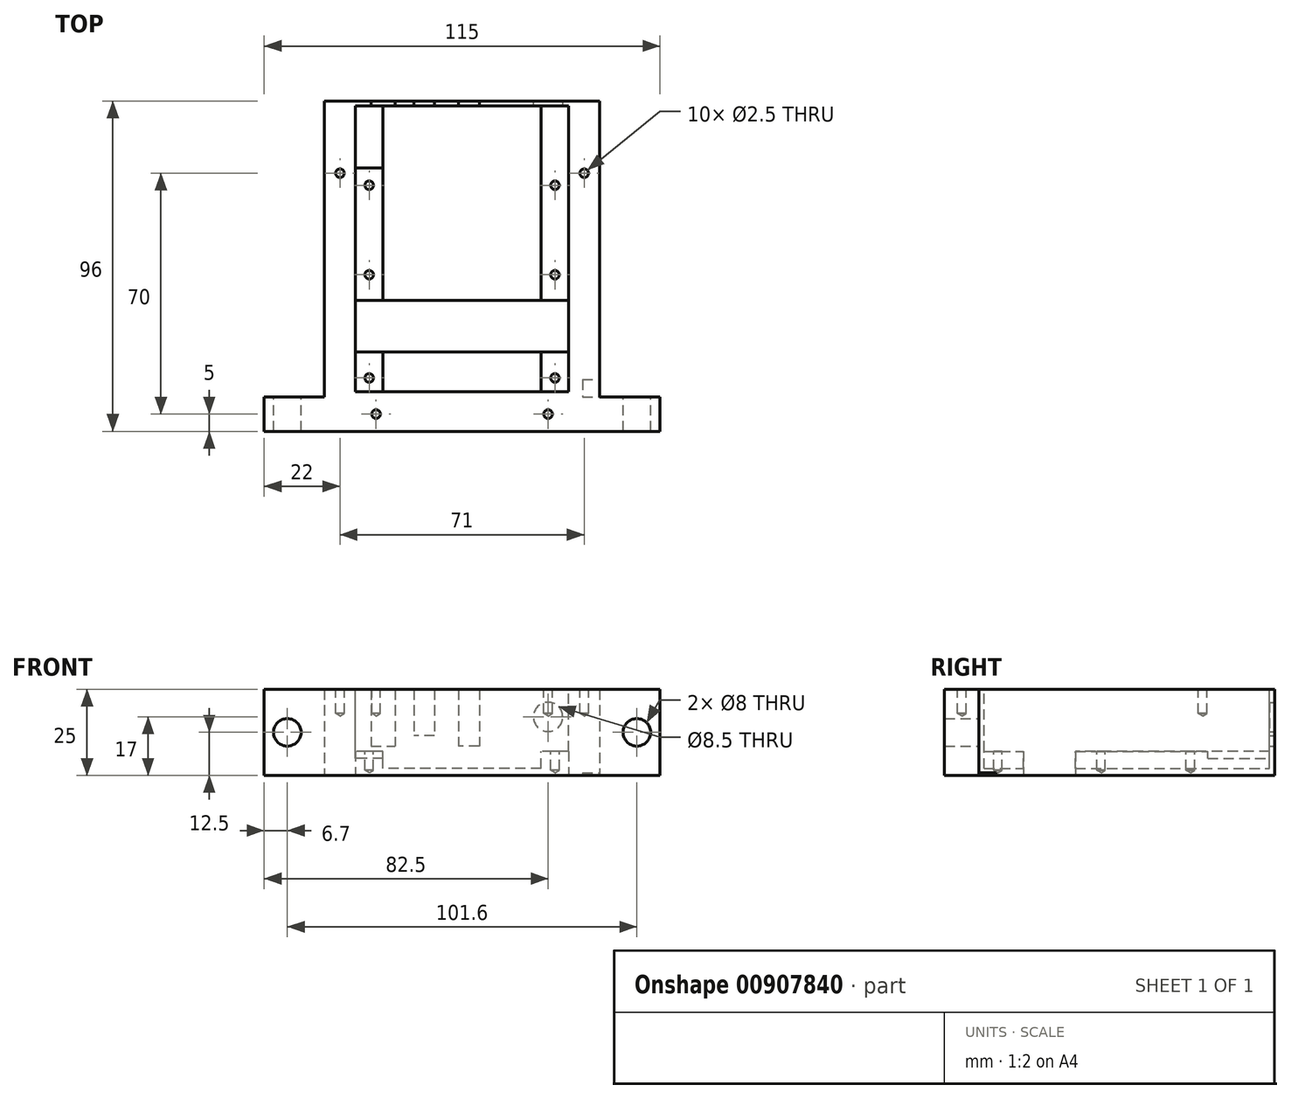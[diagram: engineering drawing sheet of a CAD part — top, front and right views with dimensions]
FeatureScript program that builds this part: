
annotation { "Feature Type Name" : "Feature", "Feature Type Description" : "" }
export const myFeature = defineFeature(function(context is Context, id is Id, definition is map)
    precondition{}
    {
        {
            var Q0;
            Q0=qCreatedBy(makeId("Top.planeOp"),FACE);
            var sketch = newSketch(context, id + "F0", { "sketchPlane" : qUnion([Q0])});
            skLineSegment(sketch, "E0.bottom", {"start": v(-40, 48) * mm, "end": v(40, 48) * mm});
            skLineSegment(sketch, "E0.left", {"start": v(-40, 48) * mm, "end": v(-40, -38) * mm});
            skLineSegment(sketch, "E0.right", {"start": v(40, 48) * mm, "end": v(40, -38) * mm});
            skLineSegment(sketch, "E1.bottom", {"start": v(-57.5, -38) * mm, "end": v(-40, -38) * mm});
            skLineSegment(sketch, "E1.top", {"start": v(-57.5, -48) * mm, "end": v(57.5, -48) * mm});
            skLineSegment(sketch, "E1.left", {"start": v(-57.5, -38) * mm, "end": v(-57.5, -48) * mm});
            skLineSegment(sketch, "E1.right", {"start": v(57.5, -38) * mm, "end": v(57.5, -48) * mm});
            skLineSegment(sketch, "E2", {"start": v(0, 66.03) * mm, "end": v(0, -67.52) * mm, "construction": true});
            skLineSegment(sketch, "E3.trimOffspring", {"start": v(40, -38) * mm, "end": v(57.5, -38) * mm});
            skLineSegment(sketch, "E4", {"start": v(-41.52, 0) * mm, "end": v(40.59, 0) * mm, "construction": true});
            skSolve(sketch);
        }
        {
            var Q0;
            Q0 = qSketchRegion(id + "F0", true);
            extrude(context, id + "F1", {"entities" : qUnion([Q0]), "depth" : 25 * mm, "offsetDistance" : 25 * mm});
        }
        {
            var Q0;
            Q0=makeQuery(id+"F1.opExtrude","CAP_FACE",FACE,{"disambiguationData":[OSD([sQuery(id+"F0.wireOp",EDGE,"E0.bottom"),sQuery(id+"F0.wireOp",EDGE,"E0.left"),sQuery(id+"F0.wireOp",EDGE,"E0.right"),sQuery(id+"F0.wireOp",EDGE,"E1.bottom"),sQuery(id+"F0.wireOp",EDGE,"E1.top"),sQuery(id+"F0.wireOp",EDGE,"E1.left"),sQuery(id+"F0.wireOp",EDGE,"E1.right"),sQuery(id+"F0.wireOp",EDGE,"E3.trimOffspring")])],"isStart":false});
            var sketch = newSketch(context, id + "F2", { "sketchPlane" : qUnion([Q0])});
            skLineSegment(sketch, "E5", {"start": v(0, 48) * mm, "end": v(0, -48) * mm, "construction": true});
            skLineSegment(sketch, "E6", {"start": v(-40, 5) * mm, "end": v(40, 5) * mm, "construction": true});
            skLineSegment(sketch, "E7.bottom", {"start": v(31, 46.5) * mm, "end": v(-31, 46.5) * mm});
            skLineSegment(sketch, "E7.top", {"start": v(31, -36.5) * mm, "end": v(-31, -36.5) * mm});
            skLineSegment(sketch, "E7.left", {"start": v(31, 46.5) * mm, "end": v(31, -36.5) * mm});
            skLineSegment(sketch, "E7.right", {"start": v(-31, 46.5) * mm, "end": v(-31, -36.5) * mm});
            skPoint(sketch, "E7.middle", {"position": v(0, 5) * mm});
            skSolve(sketch);
        }
        {
            var Q0;
            Q0=makeQuery(id+"F2.imprint","IMPRINT",FACE,{"disambiguationData":[TD([[makeQuery(id+"F2.imprint","IMPRINT",EDGE,{"derivedFrom":sQuery(id+"F2.wireOp",EDGE,"E7.bottom")}),1.0]])]});
            extrude(context, id + "F3", {"entities" : qUnion([Q0]), "operationType" : NewBodyOperationType.REMOVE, "oppositeDirection" : true, "depth" : 18 * mm, "offsetDistance" : 25 * mm});
        }
        {
            var Q0;
            Q0=makeQuery(id+"F3.boolean.opBoolean","COPY",FACE,{"derivedFrom":makeQuery(id+"F3.opExtrude","CAP_FACE",FACE,{"disambiguationData":[OSD([sQuery(id+"F2.wireOp",EDGE,"E7.bottom"),sQuery(id+"F2.wireOp",EDGE,"E7.top"),sQuery(id+"F2.wireOp",EDGE,"E7.left"),sQuery(id+"F2.wireOp",EDGE,"E7.right")])],"isStart":false})});
            var sketch = newSketch(context, id + "F4", { "sketchPlane" : qUnion([Q0])});
            skLineSegment(sketch, "E8", {"start": v(0, 46.5) * mm, "end": v(0, -36.5) * mm, "construction": true});
            skLineSegment(sketch, "E9.bottom", {"start": v(23, -36.5) * mm, "end": v(-23, -36.5) * mm});
            skLineSegment(sketch, "E9.top", {"start": v(23, 46.5) * mm, "end": v(-23, 46.5) * mm});
            skLineSegment(sketch, "E9.left", {"start": v(23, -36.5) * mm, "end": v(23, 46.5) * mm});
            skLineSegment(sketch, "E9.right", {"start": v(-23, -36.5) * mm, "end": v(-23, 46.5) * mm});
            skSolve(sketch);
        }
        {
            var Q0;
            Q0=makeQuery(id+"F4.imprint","IMPRINT",FACE,{"disambiguationData":[TD([[makeQuery(id+"F4.imprint","IMPRINT",EDGE,{"derivedFrom":sQuery(id+"F4.wireOp",EDGE,"E9.bottom")}),-1.0]])]});
            extrude(context, id + "F5", {"entities" : qUnion([Q0]), "operationType" : NewBodyOperationType.REMOVE, "oppositeDirection" : true, "depth" : 5 * mm, "offsetDistance" : 25 * mm});
        }
        {
            var Q0;
            Q0=makeQuery(id+"F3.boolean.opBoolean","COPY",FACE,{"derivedFrom":makeQuery(id+"F3.opExtrude","CAP_FACE",FACE,{"disambiguationData":[OSD([sQuery(id+"F2.wireOp",EDGE,"E7.bottom"),sQuery(id+"F2.wireOp",EDGE,"E7.top"),sQuery(id+"F2.wireOp",EDGE,"E7.left"),sQuery(id+"F2.wireOp",EDGE,"E7.right")])],"isStart":false})});
            var sketch = newSketch(context, id + "F6", { "sketchPlane" : qUnion([Q0])});
            skLineSegment(sketch, "E10", {"start": v(-27, -36.5) * mm, "end": v(-27, 28.23) * mm, "construction": true});
            skLineSegment(sketch, "E11", {"start": v(27, -36.5) * mm, "end": v(27, 26.7) * mm, "construction": true});
            skLineSegment(sketch, "E12", {"start": v(0, 28) * mm, "end": v(0, -50.3) * mm, "construction": true});
            skLineSegment(sketch, "E13", {"start": v(-29.07, 23.5) * mm, "end": v(28.49, 23.5) * mm, "construction": true});
            skLineSegment(sketch, "E14.0", {"start": v(-29.07, -2.5) * mm, "end": v(28.49, -2.5) * mm});
            skLineSegment(sketch, "E15.0", {"start": v(-29.07, -32.5) * mm, "end": v(28.49, -32.5) * mm});
            skPoint(sketch, "E16", {"position": v(-27, -32.5) * mm});
            skPoint(sketch, "E17", {"position": v(-27, 23.5) * mm});
            skPoint(sketch, "E18", {"position": v(27, 23.5) * mm});
            skPoint(sketch, "E19", {"position": v(27, -2.5) * mm});
            skPoint(sketch, "E20", {"position": v(27, -32.5) * mm});
            skPoint(sketch, "E21", {"position": v(-27, -2.5) * mm});
            skSolve(sketch);
        }
        {
            var Q0;
            Q0=sQuery(id+"F6.wireOp",VERTEX,"E16");
            var Q1;
            Q1=sQuery(id+"F6.wireOp",VERTEX,"E21");
            var Q2;
            Q2=sQuery(id+"F6.wireOp",VERTEX,"E17");
            var Q3;
            Q3=sQuery(id+"F6.wireOp",VERTEX,"E20");
            var Q4;
            Q4=sQuery(id+"F6.wireOp",VERTEX,"E19");
            var Q5;
            Q5=sQuery(id+"F6.wireOp",VERTEX,"E18");
            var Q6;
            Q6=makeQuery(id+"F1.opExtrude","SWEPT_BODY",BODY,{"disambiguationData":[OSD([sQuery(id+"F0.wireOp",EDGE,"E0.bottom"),sQuery(id+"F0.wireOp",EDGE,"E0.left"),sQuery(id+"F0.wireOp",EDGE,"E0.right"),sQuery(id+"F0.wireOp",EDGE,"E1.bottom"),sQuery(id+"F0.wireOp",EDGE,"E1.top"),sQuery(id+"F0.wireOp",EDGE,"E1.left"),sQuery(id+"F0.wireOp",EDGE,"E1.right"),sQuery(id+"F0.wireOp",EDGE,"E3.trimOffspring")])]});
            hole(context, id + "F7", {"style" : HoleStyle.SIMPLE, "endStyle" : HoleEndStyle.BLIND, "holeDiameter" : 2.5 * mm, "majorDiameter" : 5 * mm, "holeDepth" : 5.5 * mm, "isTappedThrough" : true, "tappedDepth" : 12 * mm, "tapClearance" : 3, "startFromSketch" : true, "locations" : qUnion([Q0, Q1, Q2, Q3, Q4, Q5]), "scope" : qUnion([Q6])});
        }
        {
            var Q0;
            Q0=makeQuery(id+"F1.opExtrude","CAP_FACE",FACE,{"disambiguationData":[OSD([sQuery(id+"F0.wireOp",EDGE,"E0.bottom"),sQuery(id+"F0.wireOp",EDGE,"E0.left"),sQuery(id+"F0.wireOp",EDGE,"E0.right"),sQuery(id+"F0.wireOp",EDGE,"E1.bottom"),sQuery(id+"F0.wireOp",EDGE,"E1.top"),sQuery(id+"F0.wireOp",EDGE,"E1.left"),sQuery(id+"F0.wireOp",EDGE,"E1.right"),sQuery(id+"F0.wireOp",EDGE,"E3.trimOffspring")])],"isStart":true});
            var sketch = newSketch(context, id + "F8", { "sketchPlane" : qUnion([Q0])});
            skLineSegment(sketch, "E22.bottom", {"start": v(-31, 25) * mm, "end": v(31, 25) * mm});
            skLineSegment(sketch, "E22.top", {"start": v(-31, 10) * mm, "end": v(31, 10) * mm});
            skLineSegment(sketch, "E22.left", {"start": v(-31, 25) * mm, "end": v(-31, 10) * mm});
            skLineSegment(sketch, "E22.right", {"start": v(31, 25) * mm, "end": v(31, 10) * mm});
            skPoint(sketch, "E23.endSnap0", {"position": v(0, 10) * mm});
            skLineSegment(sketch, "E24", {"start": v(0, 48) * mm, "end": v(0, 0) * mm, "construction": true});
            skSolve(sketch);
        }
        {
            var Q0;
            Q0=makeQuery(id+"F8.imprint","IMPRINT",FACE,{"disambiguationData":[TD([[makeQuery(id+"F8.imprint","IMPRINT",EDGE,{"derivedFrom":sQuery(id+"F8.wireOp",EDGE,"E22.bottom")}),-1.0]])]});
            extrude(context, id + "F9", {"entities" : qUnion([Q0]), "operationType" : NewBodyOperationType.REMOVE, "endBound" : BoundingType.THROUGH_ALL, "oppositeDirection" : true, "depth" : 25 * mm, "offsetDistance" : 25 * mm});
        }
        {
            var Q0;
            Q0=makeQuery(id+"F1.opExtrude","SWEPT_FACE",FACE,{"disambiguationData":[OSD([sQuery(id+"F0.wireOp",EDGE,"E3.trimOffspring")])]});
            var sketch = newSketch(context, id + "F10", { "sketchPlane" : qUnion([Q0])});
            skLineSegment(sketch, "E25", {"start": v(-51.24, 12.5) * mm, "end": v(51.38, 12.5) * mm, "construction": true});
            skLineSegment(sketch, "E26", {"start": v(50.8, 1.14) * mm, "end": v(50.8, 21.87) * mm, "construction": true});
            skLineSegment(sketch, "E27", {"start": v(-50.8, 2.75) * mm, "end": v(-50.8, 19.82) * mm, "construction": true});
            skLineSegment(sketch, "E28", {"start": v(0, 27.92) * mm, "end": v(0, 18.42) * mm, "construction": true});
            skPoint(sketch, "E29", {"position": v(50.8, 12.5) * mm});
            skPoint(sketch, "E30", {"position": v(-50.8, 12.5) * mm});
            skSolve(sketch);
        }
        {
            var Q0;
            Q0=sQuery(id+"F10.wireOp",VERTEX,"E29");
            var Q1;
            Q1=sQuery(id+"F10.wireOp",VERTEX,"E30");
            var Q2;
            Q2=makeQuery(id+"F1.opExtrude","SWEPT_BODY",BODY,{"disambiguationData":[OSD([sQuery(id+"F0.wireOp",EDGE,"E0.bottom"),sQuery(id+"F0.wireOp",EDGE,"E0.left"),sQuery(id+"F0.wireOp",EDGE,"E0.right"),sQuery(id+"F0.wireOp",EDGE,"E1.bottom"),sQuery(id+"F0.wireOp",EDGE,"E1.top"),sQuery(id+"F0.wireOp",EDGE,"E1.left"),sQuery(id+"F0.wireOp",EDGE,"E1.right"),sQuery(id+"F0.wireOp",EDGE,"E3.trimOffspring")])]});
            hole(context, id + "F11", {"style" : HoleStyle.SIMPLE, "endStyle" : HoleEndStyle.THROUGH, "holeDiameter" : 8 * mm, "majorDiameter" : 5 * mm, "isTappedThrough" : true, "tappedDepth" : 12 * mm, "tapClearance" : 3, "startFromSketch" : true, "locations" : qUnion([Q0, Q1]), "scope" : qUnion([Q2])});
        }
        {
            var Q0;
            Q0=makeQuery(id+"F1.opExtrude","SWEPT_FACE",FACE,{"disambiguationData":[OSD([sQuery(id+"F0.wireOp",EDGE,"E0.bottom")])]});
            var sketch = newSketch(context, id + "F12", { "sketchPlane" : qUnion([Q0])});
            skLineSegment(sketch, "E31.bottom", {"start": v(26.5, 25) * mm, "end": v(19.5, 25) * mm});
            skLineSegment(sketch, "E31.top", {"start": v(26.5, 8.5) * mm, "end": v(19.5, 8.5) * mm});
            skLineSegment(sketch, "E31.left", {"start": v(26.5, 25) * mm, "end": v(26.5, 8.5) * mm});
            skLineSegment(sketch, "E31.right", {"start": v(19.5, 25) * mm, "end": v(19.5, 8.5) * mm});
            skLineSegment(sketch, "E32.bottom", {"start": v(8, 25) * mm, "end": v(14, 25) * mm});
            skLineSegment(sketch, "E32.left", {"start": v(8, 25) * mm, "end": v(8, 11.5) * mm});
            skLineSegment(sketch, "E32.right", {"start": v(14, 25) * mm, "end": v(14, 11.5) * mm});
            skLineSegment(sketch, "E33.bottom", {"start": v(-5, 25) * mm, "end": v(1, 25) * mm});
            skLineSegment(sketch, "E33.top", {"start": v(-5, 8.5) * mm, "end": v(1, 8.5) * mm});
            skLineSegment(sketch, "E33.left", {"start": v(-5, 25) * mm, "end": v(-5, 8.5) * mm});
            skLineSegment(sketch, "E33.right", {"start": v(1, 25) * mm, "end": v(1, 8.5) * mm});
            skLineSegment(sketch, "E34", {"start": v(8, 11.5) * mm, "end": v(14, 11.5) * mm});
            skSolve(sketch);
        }
        {
            var Q0;
            Q0=makeQuery(id+"F12.imprint","IMPRINT",FACE,{"disambiguationData":[TD([[makeQuery(id+"F12.imprint","IMPRINT",EDGE,{"derivedFrom":sQuery(id+"F12.wireOp",EDGE,"E33.bottom")}),1.0]])]});
            var Q1;
            Q1=makeQuery(id+"F12.imprint","IMPRINT",FACE,{"disambiguationData":[TD([[makeQuery(id+"F12.imprint","IMPRINT",EDGE,{"derivedFrom":sQuery(id+"F12.wireOp",EDGE,"E32.bottom")}),1.0]])]});
            var Q2;
            Q2=makeQuery(id+"F12.imprint","IMPRINT",FACE,{"disambiguationData":[TD([[makeQuery(id+"F12.imprint","IMPRINT",EDGE,{"derivedFrom":sQuery(id+"F12.wireOp",EDGE,"E31.bottom")}),1.0]])]});
            var Q3;
            Q3=makeQuery(id+"F3.boolean.opBoolean","COPY",FACE,{"derivedFrom":makeQuery(id+"F3.opExtrude","SWEPT_FACE",FACE,{"disambiguationData":[OSD([sQuery(id+"F2.wireOp",EDGE,"E7.bottom")])]})});
            extrude(context, id + "F13", {"entities" : qUnion([Q0, Q1, Q2]), "operationType" : NewBodyOperationType.REMOVE, "endBound" : BoundingType.UP_TO_SURFACE, "oppositeDirection" : true, "depth" : 25 * mm, "endBoundEntityFace" : qUnion([Q3]), "offsetDistance" : 25 * mm});
        }
        {
            var Q0;
            {var subQ1=sQuery(id+"F2.wireOp",EDGE,"E7.right");var subQ2=makeQuery(id+"F3.boolean.opBoolean","COPY",FACE,{"derivedFrom":makeQuery(id+"F3.opExtrude","SWEPT_FACE",FACE,{"disambiguationData":[OSD([subQ1])]})});var subQ3=sQuery(id+"F2.wireOp",EDGE,"E7.bottom");var subQ4=makeQuery(id+"F3.boolean.opBoolean","COPY",FACE,{"derivedFrom":makeQuery(id+"F3.opExtrude","SWEPT_FACE",FACE,{"disambiguationData":[OSD([subQ3])]})});var subQ5=sQuery(id+"F2.wireOp",EDGE,"E7.top");Q0=makeQuery(id+"F9.boolean.opBoolean","SPLIT",FACE,{"disambiguationData":[TD([subQ4])],"derivedFrom":makeQuery(id+"F5.boolean.opBoolean","SPLIT",FACE,{"disambiguationData":[TD([subQ2])],"derivedFrom":makeQuery(id+"F3.boolean.opBoolean","COPY",FACE,{"derivedFrom":makeQuery(id+"F3.opExtrude","CAP_FACE",FACE,{"disambiguationData":[OSD([subQ3,subQ5,sQuery(id+"F2.wireOp",EDGE,"E7.left"),subQ1])],"isStart":false})})})});}
            var sketch = newSketch(context, id + "F14", { "sketchPlane" : qUnion([Q0])});
            skLineSegment(sketch, "E35.bottom", {"start": v(-31, 46.5) * mm, "end": v(-23, 46.5) * mm});
            skLineSegment(sketch, "E35.top", {"start": v(-31, 28.5) * mm, "end": v(-23, 28.5) * mm});
            skLineSegment(sketch, "E35.left", {"start": v(-31, 46.5) * mm, "end": v(-31, 28.5) * mm});
            skLineSegment(sketch, "E35.right", {"start": v(-23, 46.5) * mm, "end": v(-23, 28.5) * mm});
            skSolve(sketch);
        }
        {
            var Q0;
            Q0=makeQuery(id+"F14.imprint","IMPRINT",FACE,{"disambiguationData":[TD([[makeQuery(id+"F14.imprint","IMPRINT",EDGE,{"derivedFrom":sQuery(id+"F14.wireOp",EDGE,"E35.bottom")}),1.0]])]});
            extrude(context, id + "F15", {"entities" : qUnion([Q0]), "operationType" : NewBodyOperationType.REMOVE, "oppositeDirection" : true, "depth" : 2 * mm, "offsetDistance" : 25 * mm});
        }
        {
            var Q0;
            Q0=makeQuery(id+"F1.opExtrude","SWEPT_FACE",FACE,{"disambiguationData":[OSD([sQuery(id+"F0.wireOp",EDGE,"E0.bottom")])]});
            var sketch = newSketch(context, id + "F16", { "sketchPlane" : qUnion([Q0])});
            skCircle(sketch, "E36", {"center": v(-25, 17) * mm, "radius": 4.25 * mm});
            skSolve(sketch);
        }
        {
            var Q0;
            Q0=makeQuery(id+"F16.imprint","IMPRINT",FACE,{"disambiguationData":[TD([[makeQuery(id+"F16.imprint","IMPRINT",EDGE,{"derivedFrom":sQuery(id+"F16.wireOp",EDGE,"E36")}),1.0]])]});
            var Q1;
            Q1=makeQuery(id+"F15.boolean.opBoolean","MERGE",FACE,{"derivedFrom":[makeQuery(id+"F5.boolean.opBoolean","MERGE",FACE,{"derivedFrom":[makeQuery(id+"F3.boolean.opBoolean","COPY",FACE,{"derivedFrom":makeQuery(id+"F3.opExtrude","SWEPT_FACE",FACE,{"disambiguationData":[OSD([sQuery(id+"F2.wireOp",EDGE,"E7.bottom")])]})})],"fromTools":[makeQuery(id+"F5.opExtrude","SWEPT_FACE",FACE,{"disambiguationData":[OSD([sQuery(id+"F4.wireOp",EDGE,"E9.top")])]})]})],"fromTools":[makeQuery(id+"F15.opExtrude","SWEPT_FACE",FACE,{"disambiguationData":[OSD([sQuery(id+"F14.wireOp",EDGE,"E35.bottom")])]})]});
            extrude(context, id + "F17", {"entities" : qUnion([Q0]), "operationType" : NewBodyOperationType.REMOVE, "endBound" : BoundingType.UP_TO_SURFACE, "oppositeDirection" : true, "depth" : 25 * mm, "endBoundEntityFace" : qUnion([Q1]), "offsetDistance" : 25 * mm});
        }
        {
            var Q0;
            {var subQ0=sQuery(id+"FSGkL8cZMvJVaoK_1.wireOp",EDGE,"19ZCul45-CmC5-CmSV-8faD-4O6wiWYA0Wkr.top");var subQ3=sQuery(id+"F0.wireOp",EDGE,"E0.right");Q0=makeQuery(id+"FY24BLFiGkHRrBw_1.boolean.opBoolean","SPLIT",FACE,{"disambiguationData":[TD([makeQuery(id+"FY24BLFiGkHRrBw_1.opExtrude","SWEPT_FACE",FACE,{"disambiguationData":[OSD([subQ0])]})])],"derivedFrom":makeQuery(id+"F1.opExtrude","SWEPT_FACE",FACE,{"disambiguationData":[OSD([subQ3])]})});}
            var sketch = newSketch(context, id + "F18", { "sketchPlane" : qUnion([Q0])});
            skLineSegment(sketch, "E37.bottom", {"start": v(-38, 0) * mm, "end": v(-33, 0) * mm});
            skLineSegment(sketch, "E37.top", {"start": v(-38, 0.7) * mm, "end": v(-33, 0.7) * mm});
            skLineSegment(sketch, "E37.left", {"start": v(-38, 0) * mm, "end": v(-38, 0.7) * mm});
            skLineSegment(sketch, "E37.right", {"start": v(-33, 0) * mm, "end": v(-33, 0.7) * mm});
            skSolve(sketch);
        }
        {
            var Q0;
            Q0=makeQuery(id+"F18.imprint","IMPRINT",FACE,{"disambiguationData":[TD([[makeQuery(id+"F18.imprint","IMPRINT",EDGE,{"derivedFrom":sQuery(id+"F18.wireOp",EDGE,"E37.bottom")}),-1.0]])]});
            extrude(context, id + "F19", {"entities" : qUnion([Q0]), "operationType" : NewBodyOperationType.REMOVE, "oppositeDirection" : true, "depth" : 5 * mm, "offsetDistance" : 25 * mm});
        }
        {
            var Q0;
            {var subQ0=sQuery(id+"F0.wireOp",EDGE,"E3.trimOffspring");var subQ1=sQuery(id+"F0.wireOp",EDGE,"E1.right");var subQ2=sQuery(id+"F0.wireOp",EDGE,"E1.left");var subQ3=sQuery(id+"F0.wireOp",EDGE,"E1.top");var subQ4=sQuery(id+"F0.wireOp",EDGE,"E0.bottom");var subQ5=sQuery(id+"F0.wireOp",EDGE,"E1.bottom");var subQ6=sQuery(id+"F0.wireOp",EDGE,"E0.left");var subQ7=sQuery(id+"F0.wireOp",EDGE,"E0.right");Q0=makeQuery(id+"F13.boolean.opBoolean","SPLIT",FACE,{"disambiguationData":[TD([makeQuery(id+"F1.opExtrude","SWEPT_FACE",FACE,{"disambiguationData":[OSD([subQ6])]})])],"derivedFrom":makeQuery(id+"F1.opExtrude","CAP_FACE",FACE,{"disambiguationData":[OSD([subQ4,subQ6,subQ7,subQ5,subQ3,subQ2,subQ1,subQ0])],"isStart":false})});}
            var sketch = newSketch(context, id + "F20", { "sketchPlane" : qUnion([Q0])});
            skLineSegment(sketch, "E38", {"start": v(0, -48) * mm, "end": v(0, 101.86) * mm, "construction": true});
            skLineSegment(sketch, "E39", {"start": v(57.5, -43) * mm, "end": v(-57.5, -43) * mm, "construction": true});
            skLineSegment(sketch, "E40", {"start": v(31, 46.5) * mm, "end": v(40, 46.5) * mm, "construction": true});
            skLineSegment(sketch, "E41", {"start": v(31, -36.5) * mm, "end": v(40, -36.5) * mm, "construction": true});
            skLineSegment(sketch, "E42", {"start": v(35.5, 46.5) * mm, "end": v(35.5, -36.5) * mm, "construction": true});
            skLineSegment(sketch, "E43", {"start": v(-31, -36.5) * mm, "end": v(-40, -36.5) * mm, "construction": true});
            skLineSegment(sketch, "E44", {"start": v(-31, 46.5) * mm, "end": v(-40, 46.5) * mm, "construction": true});
            skLineSegment(sketch, "E45", {"start": v(-35.5, 46.5) * mm, "end": v(-35.5, -36.5) * mm, "construction": true});
            skPoint(sketch, "E46", {"position": v(25, -43) * mm});
            skPoint(sketch, "E47", {"position": v(-25, -43) * mm});
            skPoint(sketch, "E48", {"position": v(35.5, 27) * mm});
            skPoint(sketch, "E49", {"position": v(-35.5, 27) * mm});
            skSolve(sketch);
        }
        {
            var Q0;
            Q0=sQuery(id+"F20.wireOp",VERTEX,"E46");
            var Q1;
            Q1=sQuery(id+"F20.wireOp",VERTEX,"E47");
            var Q2;
            Q2=sQuery(id+"F20.wireOp",VERTEX,"E48");
            var Q3;
            Q3=sQuery(id+"F20.wireOp",VERTEX,"E49");
            var Q4;
            Q4=makeQuery(id+"F1.opExtrude","SWEPT_BODY",BODY,{"disambiguationData":[OSD([sQuery(id+"F0.wireOp",EDGE,"E0.bottom"),sQuery(id+"F0.wireOp",EDGE,"E0.left"),sQuery(id+"F0.wireOp",EDGE,"E0.right"),sQuery(id+"F0.wireOp",EDGE,"E1.bottom"),sQuery(id+"F0.wireOp",EDGE,"E1.top"),sQuery(id+"F0.wireOp",EDGE,"E1.left"),sQuery(id+"F0.wireOp",EDGE,"E1.right"),sQuery(id+"F0.wireOp",EDGE,"E3.trimOffspring")])]});
            hole(context, id + "F21", {"style" : HoleStyle.SIMPLE, "endStyle" : HoleEndStyle.BLIND, "holeDiameter" : 2.5 * mm, "majorDiameter" : 5 * mm, "holeDepth" : 7 * mm, "isTappedThrough" : true, "tappedDepth" : 12 * mm, "tapClearance" : 3, "startFromSketch" : true, "locations" : qUnion([Q0, Q1, Q2, Q3]), "scope" : qUnion([Q4])});
        }
    });
